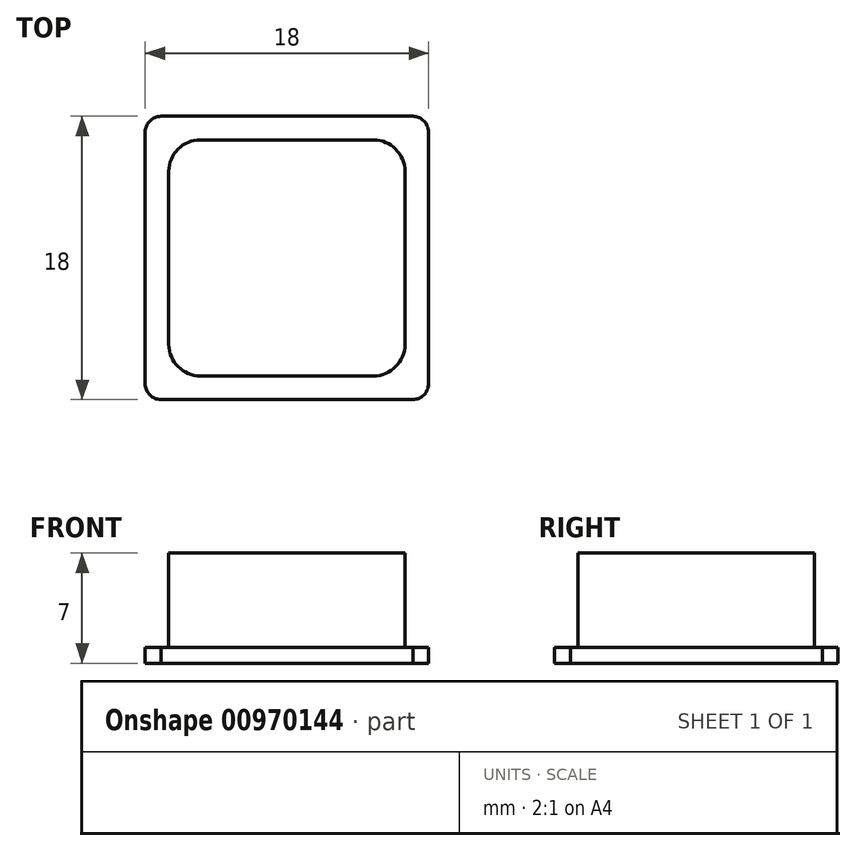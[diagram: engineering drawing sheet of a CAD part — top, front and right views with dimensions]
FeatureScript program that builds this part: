
annotation { "Feature Type Name" : "Feature", "Feature Type Description" : "" }
export const myFeature = defineFeature(function(context is Context, id is Id, definition is map)
    precondition{}
    {
        {
            var Q0;
            Q0=qCreatedBy(makeId("Top.planeOp"),FACE);
            var sketch = newSketch(context, id + "F0", { "sketchPlane" : qUnion([Q0])});
            skLineSegment(sketch, "E0.bottom", {"start": v(5.5, -7.5) * mm, "end": v(-5.5, -7.5) * mm});
            skLineSegment(sketch, "E0.top", {"start": v(5.5, 7.5) * mm, "end": v(-5.5, 7.5) * mm});
            skLineSegment(sketch, "E0.left", {"start": v(7.5, -5.5) * mm, "end": v(7.5, 5.5) * mm});
            skLineSegment(sketch, "E0.right", {"start": v(-7.5, -5.5) * mm, "end": v(-7.5, 5.5) * mm});
            skPoint(sketch, "E0.middle", {"position": v(0, 0) * mm});
            skPoint(sketch, "E1.visualSharp", {"position": v(-7.5, 7.5) * mm});
            skArc(sketch, "E1.filletArc", {"start": v(-5.5, 7.5) * mm, "mid": v(-6.91, 6.91) * mm, "end": v(-7.5, 5.5) * mm});
            skPoint(sketch, "E2.visualSharp", {"position": v(7.5, 7.5) * mm});
            skArc(sketch, "E2.filletArc", {"start": v(7.5, 5.5) * mm, "mid": v(6.91, 6.91) * mm, "end": v(5.5, 7.5) * mm});
            skPoint(sketch, "E3.visualSharp", {"position": v(7.5, -7.5) * mm});
            skArc(sketch, "E3.filletArc", {"start": v(5.5, -7.5) * mm, "mid": v(6.91, -6.91) * mm, "end": v(7.5, -5.5) * mm});
            skPoint(sketch, "E4.visualSharp", {"position": v(-7.5, -7.5) * mm});
            skArc(sketch, "E4.filletArc", {"start": v(-7.5, -5.5) * mm, "mid": v(-6.91, -6.91) * mm, "end": v(-5.5, -7.5) * mm});
            skSolve(sketch);
        }
        {
            var Q0;
            Q0 = qSketchRegion(id + "F0", true);
            extrude(context, id + "F1", {"entities" : qUnion([Q0]), "depth" : 6 * mm, "offsetDistance" : 25 * mm});
        }
        {
            var Q0;
            Q0=qCreatedBy(makeId("Top.planeOp"),FACE);
            var sketch = newSketch(context, id + "F2", { "sketchPlane" : qUnion([Q0])});
            skLineSegment(sketch, "E5.bottom", {"start": v(8, -9) * mm, "end": v(-8, -9) * mm});
            skLineSegment(sketch, "E5.top", {"start": v(8, 9) * mm, "end": v(-8, 9) * mm});
            skLineSegment(sketch, "E5.left", {"start": v(9, -8) * mm, "end": v(9, 8) * mm});
            skLineSegment(sketch, "E5.right", {"start": v(-9, -8) * mm, "end": v(-9, 8) * mm});
            skPoint(sketch, "E5.middle", {"position": v(0, 0) * mm});
            skPoint(sketch, "E6.visualSharp", {"position": v(-9, 9) * mm});
            skArc(sketch, "E6.filletArc", {"start": v(-8, 9) * mm, "mid": v(-8.7, 8.7) * mm, "end": v(-9, 8) * mm});
            skPoint(sketch, "E7.visualSharp", {"position": v(9, 9) * mm});
            skArc(sketch, "E7.filletArc", {"start": v(9, 8) * mm, "mid": v(8.7, 8.7) * mm, "end": v(8, 9) * mm});
            skPoint(sketch, "E8.visualSharp", {"position": v(9, -9) * mm});
            skArc(sketch, "E8.filletArc", {"start": v(8, -9) * mm, "mid": v(8.7, -8.7) * mm, "end": v(9, -8) * mm});
            skPoint(sketch, "E9.visualSharp", {"position": v(-9, -9) * mm});
            skArc(sketch, "E9.filletArc", {"start": v(-9, -8) * mm, "mid": v(-8.7, -8.7) * mm, "end": v(-8, -9) * mm});
            skSolve(sketch);
        }
        {
            var Q0;
            Q0=makeQuery(id+"F2.imprint","IMPRINT",FACE,{"disambiguationData":[TD([[makeQuery(id+"F2.imprint","IMPRINT",EDGE,{"derivedFrom":sQuery(id+"F2.wireOp",EDGE,"E5.bottom")}),-1.0]])]});
            extrude(context, id + "F3", {"entities" : qUnion([Q0]), "depth" : 1 * mm, "offsetDistance" : 25 * mm});
        }
        {
            var Q0;
            Q0=makeQuery(id+"F3.opExtrude","SWEPT_BODY",BODY,{"disambiguationData":[OSD([sQuery(id+"F2.wireOp",EDGE,"E5.bottom"),sQuery(id+"F2.wireOp",EDGE,"E5.top"),sQuery(id+"F2.wireOp",EDGE,"E5.left"),sQuery(id+"F2.wireOp",EDGE,"E5.right"),sQuery(id+"F2.wireOp",EDGE,"E6.filletArc"),sQuery(id+"F2.wireOp",EDGE,"E7.filletArc"),sQuery(id+"F2.wireOp",EDGE,"E8.filletArc"),sQuery(id+"F2.wireOp",EDGE,"E9.filletArc")])]});
            transform(context, id + "F4", {"entities" : qUnion([Q0]), "transformType" : TransformType.TRANSLATION_3D, "dx" : 0 * mm, "dy" : 0 * mm, "dz" : -1 * mm, "makeCopy" : false});
        }
        {
            var Q0;
            Q0=makeQuery(id+"F3.opExtrude","CAP_FACE",FACE,{"disambiguationData":[OSD([sQuery(id+"F2.wireOp",EDGE,"E5.bottom"),sQuery(id+"F2.wireOp",EDGE,"E5.top"),sQuery(id+"F2.wireOp",EDGE,"E5.left"),sQuery(id+"F2.wireOp",EDGE,"E5.right"),sQuery(id+"F2.wireOp",EDGE,"E6.filletArc"),sQuery(id+"F2.wireOp",EDGE,"E7.filletArc"),sQuery(id+"F2.wireOp",EDGE,"E8.filletArc"),sQuery(id+"F2.wireOp",EDGE,"E9.filletArc")])],"isStart":true});
            shell(context, id + "F5", {"entities" : qUnion([Q0]), "thickness" : 1 * mm});
        }
    });
